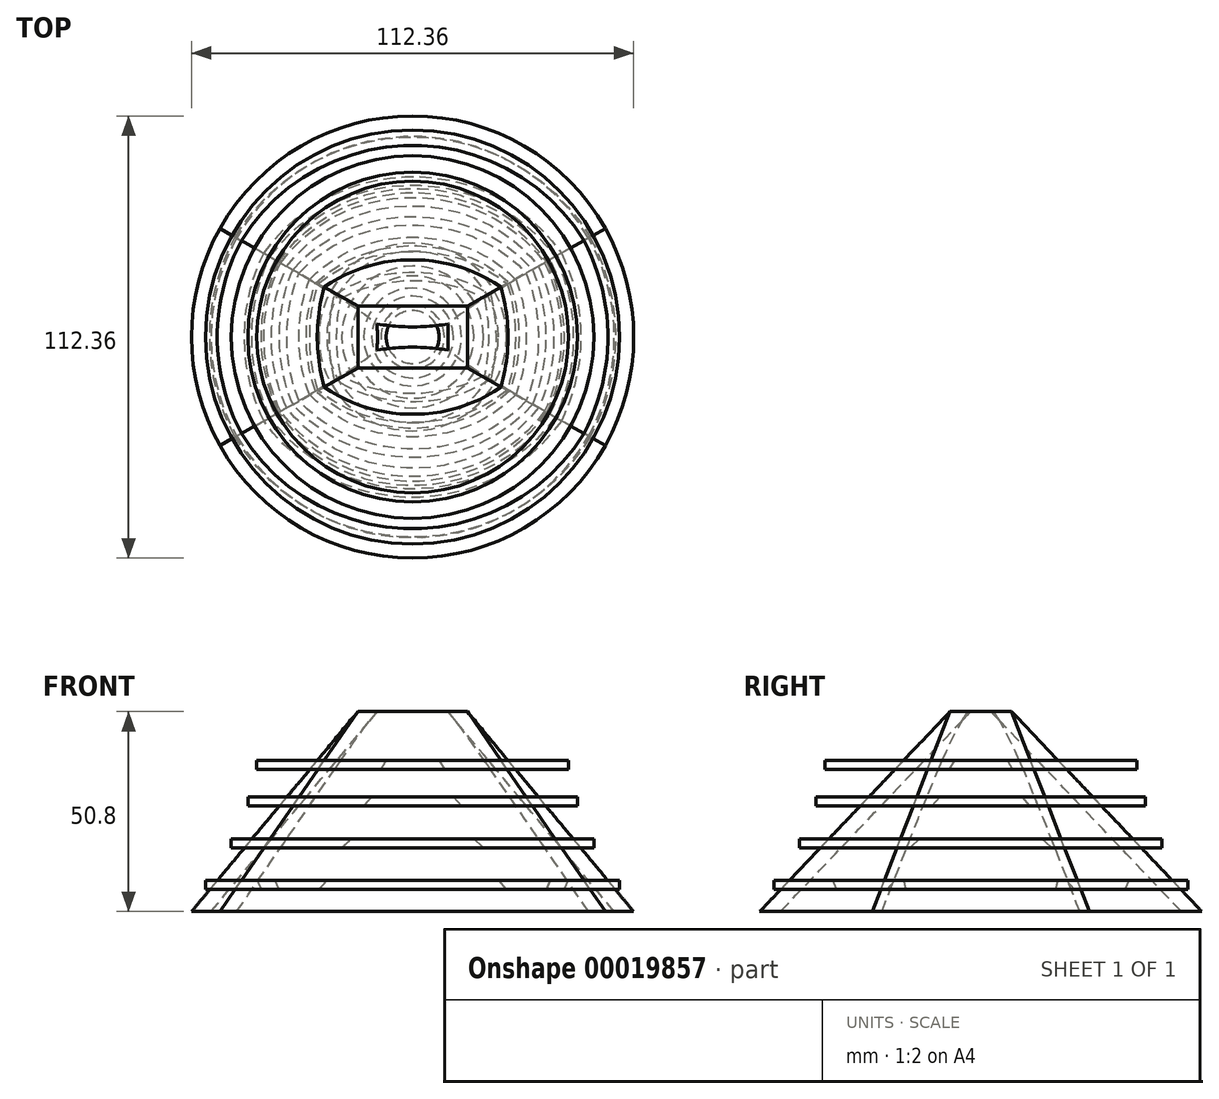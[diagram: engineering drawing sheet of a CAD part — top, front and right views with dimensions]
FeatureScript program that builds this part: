
annotation { "Feature Type Name" : "Feature", "Feature Type Description" : "" }
export const myFeature = defineFeature(function(context is Context, id is Id, definition is map)
    precondition{}
    {
        {
            var Q0;
            Q0=qCreatedBy(makeId("Top.planeOp"),FACE);
            cPlane(context, id + "F0", {"entities" : qUnion([Q0]), "cplaneType" : CPlaneType.OFFSET, "offset" : 50.8 * mm, "width" : 152.4 * mm, "height" : 152.4 * mm});
        }
        {
            var Q0;
            Q0=qCreatedBy(id+"F0.planeOp",FACE);
            var sketch = newSketch(context, id + "F1", { "sketchPlane" : qUnion([Q0])});
            skLineSegment(sketch, "E0.rect.bottom", {"start": v(-13.9, -7.83) * mm, "end": v(13.9, -7.83) * mm});
            skLineSegment(sketch, "E0.rect.top", {"start": v(-13.9, 7.83) * mm, "end": v(13.9, 7.83) * mm});
            skLineSegment(sketch, "E0.rect.left", {"start": v(-13.9, -7.83) * mm, "end": v(-13.9, 7.83) * mm});
            skLineSegment(sketch, "E0.rect.right", {"start": v(13.9, -7.83) * mm, "end": v(13.9, 7.83) * mm});
            skPoint(sketch, "E0.rect.middle", {"position": v(0, 0) * mm});
            skSolve(sketch);
        }
        {
            var Q0;
            Q0=qCreatedBy(makeId("Top.planeOp"),FACE);
            var sketch = newSketch(context, id + "F2", { "sketchPlane" : qUnion([Q0])});
            skLineSegment(sketch, "E1", {"start": v(0, 0) * mm, "end": v(-48.95, 27.57) * mm, "construction": true});
            skLineSegment(sketch, "E2", {"start": v(0, 0) * mm, "end": v(48.95, 27.57) * mm, "construction": true});
            skLineSegment(sketch, "E3", {"start": v(0, 0) * mm, "end": v(48.95, -27.57) * mm, "construction": true});
            skLineSegment(sketch, "E4", {"start": v(0, 0) * mm, "end": v(-48.95, -27.57) * mm, "construction": true});
            skArc(sketch, "E5", {"start": v(-48.95, 27.57) * mm, "mid": v(-56.18, 0) * mm, "end": v(-48.95, -27.57) * mm});
            skArc(sketch, "E6", {"start": v(48.95, 27.57) * mm, "mid": v(0, 56.18) * mm, "end": v(-48.95, 27.57) * mm});
            skArc(sketch, "E7", {"start": v(48.95, -27.57) * mm, "mid": v(56.18, 0) * mm, "end": v(48.95, 27.57) * mm});
            skArc(sketch, "E8", {"start": v(-48.95, -27.57) * mm, "mid": v(0, -56.18) * mm, "end": v(48.95, -27.57) * mm});
            skSolve(sketch);
        }
        {
            var Q0;
            Q0=makeQuery(id+"F2.imprint","IMPRINT",FACE,{"disambiguationData":[TD([[makeQuery(id+"F2.imprint","IMPRINT",EDGE,{"derivedFrom":sQuery(id+"F2.wireOp",EDGE,"E5")}),1.0]])]});
            var Q1;
            Q1=makeQuery(id+"F1.imprint","IMPRINT",FACE,{"disambiguationData":[TD([[makeQuery(id+"F1.imprint","IMPRINT",EDGE,{"derivedFrom":sQuery(id+"F1.wireOp",EDGE,"E0.rect.bottom")}),1.0]])]});
            var Q2;
            Q2=sQuery(id+"F2.wireOp",EDGE,"E6");
            var Q3;
            Q3=sQuery(id+"F2.wireOp",EDGE,"E7");
            var Q4;
            Q4=sQuery(id+"F2.wireOp",EDGE,"E8");
            var Q5;
            Q5=sQuery(id+"F2.wireOp",EDGE,"E5");
            var Q6;
            Q6=sQuery(id+"F1.wireOp",EDGE,"E0.rect.top");
            var Q7;
            Q7=sQuery(id+"F1.wireOp",EDGE,"E0.rect.right");
            var Q8;
            Q8=sQuery(id+"F1.wireOp",EDGE,"E0.rect.bottom");
            var Q9;
            Q9=makeQuery(id+"F1.imprint","IMPRINT",FACE,{"disambiguationData":[TD([[makeQuery(id+"F1.imprint","IMPRINT",EDGE,{"derivedFrom":sQuery(id+"F1.wireOp",EDGE,"E0.rect.bottom")}),1.0]])]});
            var Q10;
            Q10=sQuery(id+"F1.wireOp",EDGE,"E0.rect.left");
            loft(context, id + "F3", {"sheetProfilesArray" : [{ "sheetProfileEntities" : qUnion([Q0]) }, { "sheetProfileEntities" : qUnion([Q1]) }], "wireProfilesArray" : [{ "wireProfileEntities" : qUnion([Q2]) }, { "wireProfileEntities" : qUnion([Q3]) }, { "wireProfileEntities" : qUnion([Q4]) }, { "wireProfileEntities" : qUnion([Q5]) }, { "wireProfileEntities" : qUnion([Q6]) }, { "wireProfileEntities" : qUnion([Q7]) }, { "wireProfileEntities" : qUnion([Q8]) }, { "wireProfileEntities" : qUnion([Q9]) }, { "wireProfileEntities" : qUnion([Q10]) }]});
        }
        {
            var Q0;
            Q0=makeQuery(id+"F3.opLoft","CAP_FACE",FACE,{"disambiguationData":[OSD([makeQuery(id+"F2.imprint","IMPRINT",FACE,{"disambiguationData":[TD([[makeQuery(id+"F2.imprint","IMPRINT",EDGE,{"derivedFrom":sQuery(id+"F2.wireOp",EDGE,"E5")}),1.0]])]})])],"isStart":true});
            var Q1;
            Q1=makeQuery(id+"F3.opLoft","CAP_FACE",FACE,{"disambiguationData":[OSD([makeQuery(id+"F1.imprint","IMPRINT",FACE,{"disambiguationData":[TD([[makeQuery(id+"F1.imprint","IMPRINT",EDGE,{"derivedFrom":sQuery(id+"F1.wireOp",EDGE,"E0.rect.bottom")}),1.0]])]})])],"isStart":true});
            shell(context, id + "F4", {"entities" : qUnion([Q0, Q1]), "thickness" : 3.8 * mm});
        }
        {
            var Q0;
            Q0=qCreatedBy(makeId("Front.planeOp"),FACE);
            var sketch = newSketch(context, id + "F5", { "sketchPlane" : qUnion([Q0])});
            skLineSegment(sketch, "E9", {"start": v(0, 0) * mm, "end": v(0, 50.78) * mm, "construction": true});
            skLineSegment(sketch, "E10", {"start": v(6.72, 38.4) * mm, "end": v(8.07, 36.14) * mm});
            skLineSegment(sketch, "E11", {"start": v(6.72, 38.4) * mm, "end": v(39.6, 38.4) * mm});
            skLineSegment(sketch, "E12", {"start": v(8.07, 36.14) * mm, "end": v(39.6, 36.14) * mm});
            skLineSegment(sketch, "E13", {"start": v(39.6, 38.4) * mm, "end": v(39.6, 36.14) * mm});
            skLineSegment(sketch, "E14", {"start": v(10.38, 29.12) * mm, "end": v(12.43, 26.85) * mm});
            skLineSegment(sketch, "E15", {"start": v(10.38, 29.12) * mm, "end": v(41.86, 29.12) * mm});
            skLineSegment(sketch, "E16", {"start": v(41.86, 29.12) * mm, "end": v(41.86, 26.85) * mm});
            skLineSegment(sketch, "E17", {"start": v(12.43, 26.85) * mm, "end": v(41.86, 26.85) * mm});
            skLineSegment(sketch, "E18", {"start": v(15.55, 18.46) * mm, "end": v(18, 16.2) * mm});
            skLineSegment(sketch, "E19", {"start": v(15.55, 18.46) * mm, "end": v(46.06, 18.46) * mm});
            skLineSegment(sketch, "E20", {"start": v(18, 16.2) * mm, "end": v(46.06, 16.2) * mm});
            skLineSegment(sketch, "E21", {"start": v(46.06, 18.46) * mm, "end": v(46.06, 16.2) * mm});
            skLineSegment(sketch, "E22", {"start": v(21.78, 7.88) * mm, "end": v(23.83, 5.62) * mm});
            skLineSegment(sketch, "E23", {"start": v(21.78, 7.88) * mm, "end": v(52.61, 7.88) * mm});
            skLineSegment(sketch, "E24", {"start": v(23.83, 5.62) * mm, "end": v(52.61, 5.62) * mm});
            skLineSegment(sketch, "E25", {"start": v(52.61, 7.88) * mm, "end": v(52.61, 5.62) * mm});
            skSolve(sketch);
        }
        {
            var Q0;
            Q0=qSketchRegion(id+"F5",true);
            var Q1;
            Q1=sQuery(id+"F5.wireOp",EDGE,"E9");
            revolve(context, id + "F6", {"entities" : qUnion([Q0]), "axis" : qUnion([Q1]), "revolveType" : RevolveType.FULL});
        }
        {
            var Q0;
            Q0=makeQuery(id+"F3.opLoft","SWEPT_BODY",BODY,{"disambiguationData":[OSD([makeQuery(id+"F1.imprint","IMPRINT",FACE,{"disambiguationData":[TD([[makeQuery(id+"F1.imprint","IMPRINT",EDGE,{"derivedFrom":sQuery(id+"F1.wireOp",EDGE,"E0.rect.bottom")}),1.0]])]}),makeQuery(id+"F2.imprint","IMPRINT",FACE,{"disambiguationData":[TD([[makeQuery(id+"F2.imprint","IMPRINT",EDGE,{"derivedFrom":sQuery(id+"F2.wireOp",EDGE,"E5")}),1.0]])]})])]});
            var Q1;
            Q1=makeQuery(id+"F6.opRevolve","SWEPT_BODY",BODY,{"disambiguationData":[OSD([sQuery(id+"F5.wireOp",EDGE,"E10"),sQuery(id+"F5.wireOp",EDGE,"E11"),sQuery(id+"F5.wireOp",EDGE,"E12"),sQuery(id+"F5.wireOp",EDGE,"E13")])]});
            var Q2;
            Q2=makeQuery(id+"F6.opRevolve","SWEPT_BODY",BODY,{"disambiguationData":[OSD([sQuery(id+"F5.wireOp",EDGE,"E14"),sQuery(id+"F5.wireOp",EDGE,"E15"),sQuery(id+"F5.wireOp",EDGE,"E16"),sQuery(id+"F5.wireOp",EDGE,"E17")])]});
            var Q3;
            Q3=makeQuery(id+"F6.opRevolve","SWEPT_BODY",BODY,{"disambiguationData":[OSD([sQuery(id+"F5.wireOp",EDGE,"E18"),sQuery(id+"F5.wireOp",EDGE,"E19"),sQuery(id+"F5.wireOp",EDGE,"E20"),sQuery(id+"F5.wireOp",EDGE,"E21")])]});
            var Q4;
            Q4=makeQuery(id+"F6.opRevolve","SWEPT_BODY",BODY,{"disambiguationData":[OSD([sQuery(id+"F5.wireOp",EDGE,"E22"),sQuery(id+"F5.wireOp",EDGE,"E23"),sQuery(id+"F5.wireOp",EDGE,"E24"),sQuery(id+"F5.wireOp",EDGE,"E25")])]});
            booleanBodies(context, id + "F7", {"operationType" : BooleanOperationType.SUBTRACTION, "tools" : qUnion([Q0]), "targets" : qUnion([Q1, Q2, Q3, Q4]), "keepTools" : true});
        }
        {
            var Q0;
            Q0=makeQuery(id+"F7.opBoolean","INTERSECT",EDGE,{"derivedFrom":[makeQuery(id+"F4.opShell","OFFSET_FACE",FACE,{"disambiguationData":[OSD([sQuery(id+"F1.wireOp",EDGE,"E0.rect.bottom"),sQuery(id+"F1.wireOp",EDGE,"E0.rect.left"),sQuery(id+"F1.wireOp",EDGE,"E0.rect.right"),sQuery(id+"F2.wireOp",EDGE,"E5"),sQuery(id+"F2.wireOp",EDGE,"E7"),sQuery(id+"F2.wireOp",EDGE,"E8")])]}),makeQuery(id+"F6.opRevolve","SWEPT_FACE",FACE,{"disambiguationData":[OSD([sQuery(id+"F5.wireOp",EDGE,"E24")])]})]});
            var Q1;
            Q1=makeQuery(id+"F7.opBoolean","INTERSECT",EDGE,{"derivedFrom":[makeQuery(id+"F4.opShell","OFFSET_FACE",FACE,{"disambiguationData":[OSD([sQuery(id+"F1.wireOp",EDGE,"E0.rect.bottom"),sQuery(id+"F1.wireOp",EDGE,"E0.rect.top"),sQuery(id+"F1.wireOp",EDGE,"E0.rect.left"),sQuery(id+"F2.wireOp",EDGE,"E5"),sQuery(id+"F2.wireOp",EDGE,"E6"),sQuery(id+"F2.wireOp",EDGE,"E8")])]}),makeQuery(id+"F6.opRevolve","SWEPT_FACE",FACE,{"disambiguationData":[OSD([sQuery(id+"F5.wireOp",EDGE,"E24")])]})]});
            var Q2;
            Q2=makeQuery(id+"F7.opBoolean","INTERSECT",EDGE,{"derivedFrom":[makeQuery(id+"F4.opShell","OFFSET_FACE",FACE,{"disambiguationData":[OSD([sQuery(id+"F1.wireOp",EDGE,"E0.rect.top"),sQuery(id+"F1.wireOp",EDGE,"E0.rect.left"),sQuery(id+"F1.wireOp",EDGE,"E0.rect.right"),sQuery(id+"F2.wireOp",EDGE,"E5"),sQuery(id+"F2.wireOp",EDGE,"E6"),sQuery(id+"F2.wireOp",EDGE,"E7")])]}),makeQuery(id+"F6.opRevolve","SWEPT_FACE",FACE,{"disambiguationData":[OSD([sQuery(id+"F5.wireOp",EDGE,"E24")])]})]});
            var Q3;
            Q3=makeQuery(id+"F7.opBoolean","INTERSECT",EDGE,{"derivedFrom":[makeQuery(id+"F4.opShell","OFFSET_FACE",FACE,{"disambiguationData":[OSD([sQuery(id+"F1.wireOp",EDGE,"E0.rect.bottom"),sQuery(id+"F1.wireOp",EDGE,"E0.rect.top"),sQuery(id+"F1.wireOp",EDGE,"E0.rect.right"),sQuery(id+"F2.wireOp",EDGE,"E6"),sQuery(id+"F2.wireOp",EDGE,"E7"),sQuery(id+"F2.wireOp",EDGE,"E8")])]}),makeQuery(id+"F6.opRevolve","SWEPT_FACE",FACE,{"disambiguationData":[OSD([sQuery(id+"F5.wireOp",EDGE,"E24")])]})]});
            chamfer(context, id + "F8", {"entities" : qUnion([Q0, Q1, Q2, Q3]), "width" : 3.8 * mm, "tangentPropagation" : true});
        }
    });
